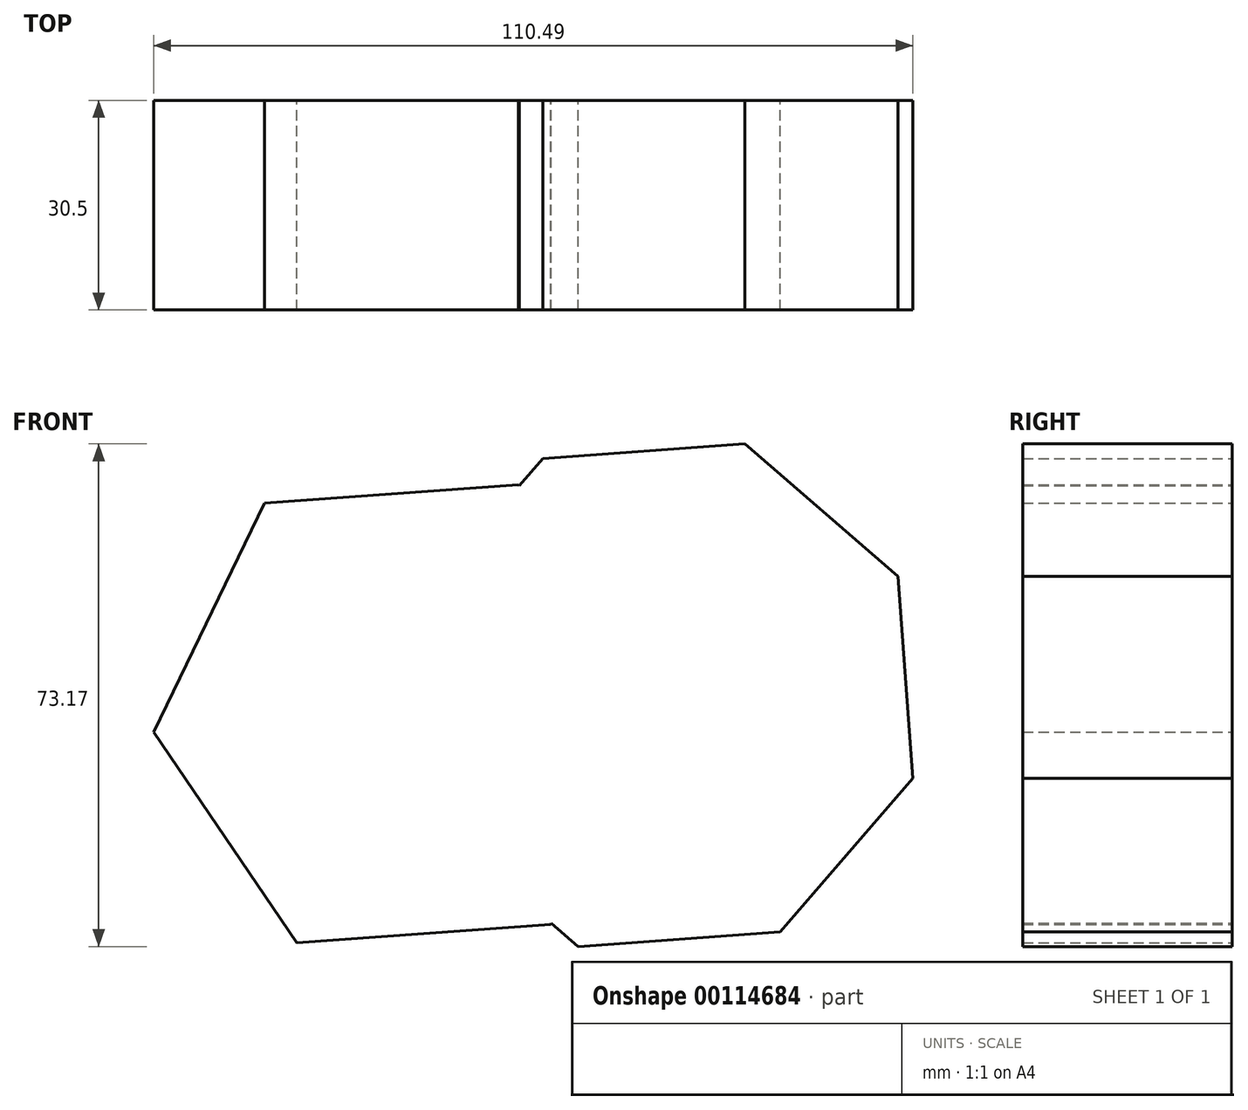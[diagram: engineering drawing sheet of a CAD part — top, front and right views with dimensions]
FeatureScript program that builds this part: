
annotation { "Feature Type Name" : "Feature", "Feature Type Description" : "" }
export const myFeature = defineFeature(function(context is Context, id is Id, definition is map)
    precondition{}
    {
        {
            var Q0;
            Q0=qCreatedBy(makeId("Front.planeOp"),FACE);
            var sketch = newSketch(context, id + "F0", { "sketchPlane" : qUnion([Q0])});
            skCircle(sketch, "E0.cCircle", {"center": v(0, 0) * mm, "radius": 32.09 * mm, "construction": true});
            skLineSegment(sketch, "E0.0", {"start": v(16.14, 33.35) * mm, "end": v(36.95, 2.7) * mm});
            skLineSegment(sketch, "E0.1", {"start": v(36.95, 2.7) * mm, "end": v(20.81, -30.66) * mm});
            skLineSegment(sketch, "E0.2", {"start": v(20.81, -30.66) * mm, "end": v(-16.14, -33.35) * mm});
            skLineSegment(sketch, "E0.3", {"start": v(-16.14, -33.35) * mm, "end": v(-36.95, -2.7) * mm});
            skLineSegment(sketch, "E0.4", {"start": v(-36.95, -2.7) * mm, "end": v(-20.81, 30.66) * mm});
            skLineSegment(sketch, "E0.5", {"start": v(-20.81, 30.66) * mm, "end": v(16.14, 33.35) * mm});
            skPoint(sketch, "E0.0.midPoint", {"position": v(26.55, 18.02) * mm});
            skCircle(sketch, "E1.cCircle", {"center": v(36.95, 2.7) * mm, "radius": 35.6 * mm, "construction": true});
            skLineSegment(sketch, "E1.0", {"start": v(54.26, -31.74) * mm, "end": v(24.84, -33.89) * mm});
            skLineSegment(sketch, "E1.1", {"start": v(24.84, -33.89) * mm, "end": v(2.52, -14.6) * mm});
            skLineSegment(sketch, "E1.2", {"start": v(2.52, -14.6) * mm, "end": v(0.37, 14.81) * mm});
            skLineSegment(sketch, "E1.3", {"start": v(0.37, 14.81) * mm, "end": v(19.65, 37.13) * mm});
            skLineSegment(sketch, "E1.4", {"start": v(19.65, 37.13) * mm, "end": v(49.07, 39.28) * mm});
            skLineSegment(sketch, "E1.5", {"start": v(49.07, 39.28) * mm, "end": v(71.4, 20) * mm});
            skLineSegment(sketch, "E1.6", {"start": v(71.4, 20) * mm, "end": v(73.54, -9.42) * mm});
            skLineSegment(sketch, "E1.7", {"start": v(73.54, -9.42) * mm, "end": v(54.26, -31.74) * mm});
            skPoint(sketch, "E1.0.midPoint", {"position": v(39.55, -32.81) * mm});
            skSolve(sketch);
        }
        {
            var Q0;
            Q0 = qSketchRegion(id + "F0", true);
            extrude(context, id + "F1", {"entities" : qUnion([Q0]), "depth" : 15 * mm, "hasSecondDirection" : true, "secondDirectionOppositeDirection" : true, "secondDirectionDepth" : 15.5 * mm});
        }
    });
